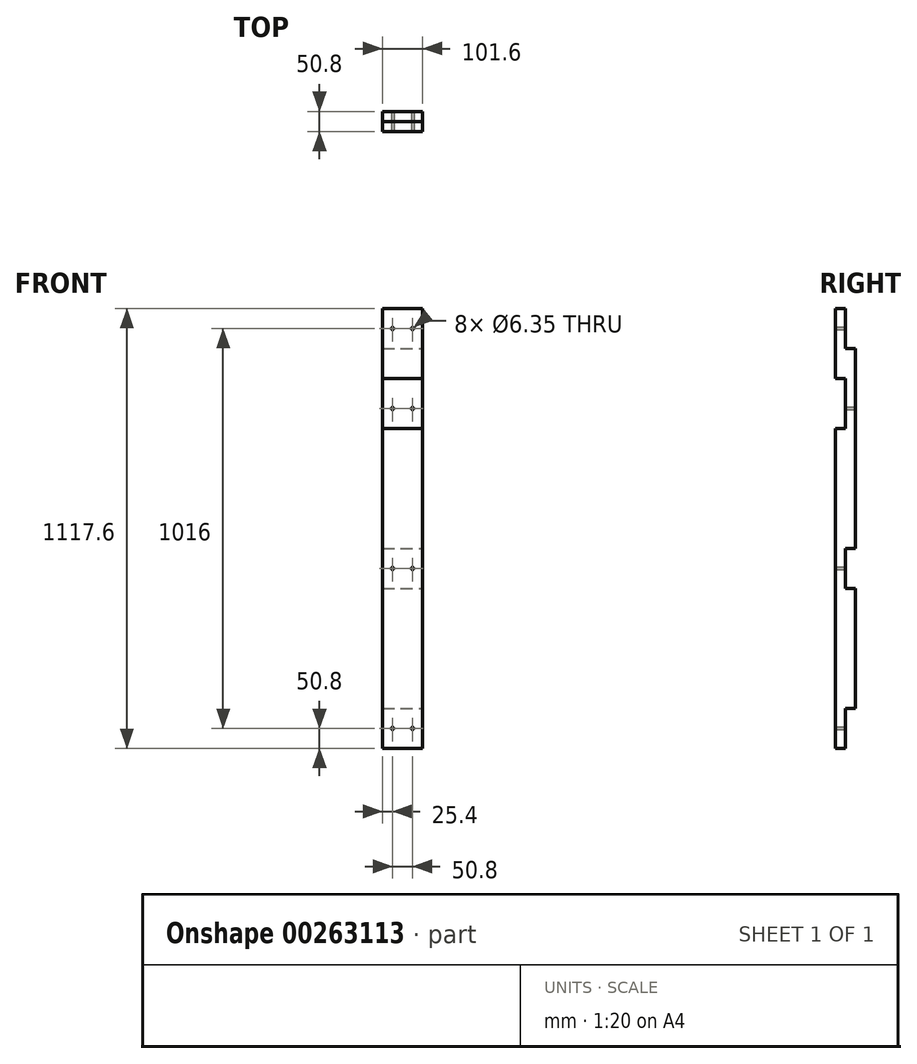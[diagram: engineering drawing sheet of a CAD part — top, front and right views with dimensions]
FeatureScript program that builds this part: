
annotation { "Feature Type Name" : "Feature", "Feature Type Description" : "" }
export const myFeature = defineFeature(function(context is Context, id is Id, definition is map)
    precondition{}
    {
        {
            var Q0;
            Q0=qCreatedBy(makeId("Top.planeOp"),FACE);
            var sketch = newSketch(context, id + "F0", { "sketchPlane" : qUnion([Q0])});
            skLineSegment(sketch, "E0.bottom", {"start": v(50.8, 25.4) * mm, "end": v(-50.8, 25.4) * mm});
            skLineSegment(sketch, "E0.top", {"start": v(50.8, -25.4) * mm, "end": v(-50.8, -25.4) * mm});
            skLineSegment(sketch, "E0.left", {"start": v(50.8, 25.4) * mm, "end": v(50.8, -25.4) * mm});
            skLineSegment(sketch, "E0.right", {"start": v(-50.8, 25.4) * mm, "end": v(-50.8, -25.4) * mm});
            skPoint(sketch, "E0.middle", {"position": v(0, 0) * mm});
            skSolve(sketch);
        }
        {
            var Q0;
            Q0 = qSketchRegion(id + "F0", true);
            extrude(context, id + "F1", {"entities" : qUnion([Q0]), "flatOperationType" : FlatOperationType.REMOVE, "offsetDistance" : 25.4 * mm, "depth" : 1117.6 * mm, "domain" : OperationDomain.MODEL});
        }
        {
            var Q0;
            Q0=makeQuery(id+"F1.opExtrude","SWEPT_FACE",FACE,{"disambiguationData":[OSD([sQuery(id+"F0.wireOp",EDGE,"E0.left")])]});
            var sketch = newSketch(context, id + "F2", { "sketchPlane" : qUnion([Q0])});
            skLineSegment(sketch, "E1.bottom", {"start": v(0, 406.4) * mm, "end": v(25.4, 406.4) * mm});
            skLineSegment(sketch, "E1.top", {"start": v(0, 508) * mm, "end": v(25.4, 508) * mm});
            skLineSegment(sketch, "E1.left", {"start": v(0, 406.4) * mm, "end": v(0, 508) * mm});
            skLineSegment(sketch, "E1.right", {"start": v(25.4, 406.4) * mm, "end": v(25.4, 508) * mm});
            skLineSegment(sketch, "E2.bottom", {"start": v(0, 101.6) * mm, "end": v(25.4, 101.6) * mm});
            skLineSegment(sketch, "E2.top", {"start": v(0, 0) * mm, "end": v(25.4, 0) * mm});
            skLineSegment(sketch, "E2.left", {"start": v(0, 101.6) * mm, "end": v(0, 0) * mm});
            skLineSegment(sketch, "E2.right", {"start": v(25.4, 101.6) * mm, "end": v(25.4, 0) * mm});
            skPoint(sketch, "E3.oppositeSnap0", {"position": v(0, 1117.6) * mm});
            skLineSegment(sketch, "E3.bottom", {"start": v(25.4, 1117.6) * mm, "end": v(0, 1117.6) * mm});
            skLineSegment(sketch, "E3.top", {"start": v(25.4, 1016) * mm, "end": v(0, 1016) * mm});
            skLineSegment(sketch, "E3.left", {"start": v(25.4, 1117.6) * mm, "end": v(25.4, 1016) * mm});
            skLineSegment(sketch, "E3.right", {"start": v(0, 1117.6) * mm, "end": v(0, 1016) * mm});
            skLineSegment(sketch, "E4.bottom", {"start": v(0, 939.8) * mm, "end": v(-25.4, 939.8) * mm});
            skLineSegment(sketch, "E4.top", {"start": v(0, 812.8) * mm, "end": v(-25.4, 812.8) * mm});
            skLineSegment(sketch, "E4.left", {"start": v(-25.4, 939.8) * mm, "end": v(-25.4, 812.8) * mm});
            skLineSegment(sketch, "E4.right", {"start": v(0, 939.8) * mm, "end": v(0, 812.8) * mm});
            skSolve(sketch);
        }
        {
            var Q0;
            Q0 = qSketchRegion(id + "F2", true);
            extrude(context, id + "F3", {"entities" : qUnion([Q0]), "operationType" : NewBodyOperationType.REMOVE, "flatOperationType" : FlatOperationType.REMOVE, "endBound" : BoundingType.THROUGH_ALL, "oppositeDirection" : true, "offsetDistance" : 25.4 * mm, "depth" : 25.4 * mm, "domain" : OperationDomain.MODEL});
        }
        {
            var Q0;
            Q0=makeQuery(id+"F1.opExtrude","SWEPT_FACE",FACE,{"disambiguationData":[OSD([sQuery(id+"F0.wireOp",EDGE,"E0.top")])]});
            var sketch = newSketch(context, id + "F4", { "sketchPlane" : qUnion([Q0])});
            skCircle(sketch, "E5", {"center": v(-25.4, 1066.8) * mm, "radius": 3.18 * mm});
            skCircle(sketch, "E6", {"center": v(-25.4, 457.2) * mm, "radius": 3.18 * mm});
            skCircle(sketch, "E7", {"center": v(-25.4, 50.8) * mm, "radius": 3.18 * mm});
            skCircle(sketch, "E8", {"center": v(25.4, 1066.8) * mm, "radius": 3.18 * mm});
            skCircle(sketch, "E9", {"center": v(25.4, 457.2) * mm, "radius": 3.18 * mm});
            skCircle(sketch, "E10", {"center": v(25.4, 50.8) * mm, "radius": 3.18 * mm});
            skCircle(sketch, "E11", {"center": v(-25.4, 863.6) * mm, "radius": 3.18 * mm});
            skCircle(sketch, "E12", {"center": v(25.4, 863.6) * mm, "radius": 3.18 * mm});
            skSolve(sketch);
        }
        {
            var Q0;
            Q0 = qSketchRegion(id + "F4", true);
            extrude(context, id + "F5", {"entities" : qUnion([Q0]), "operationType" : NewBodyOperationType.REMOVE, "endBound" : BoundingType.THROUGH_ALL, "oppositeDirection" : true, "depth" : 25.4 * mm});
        }
    });
